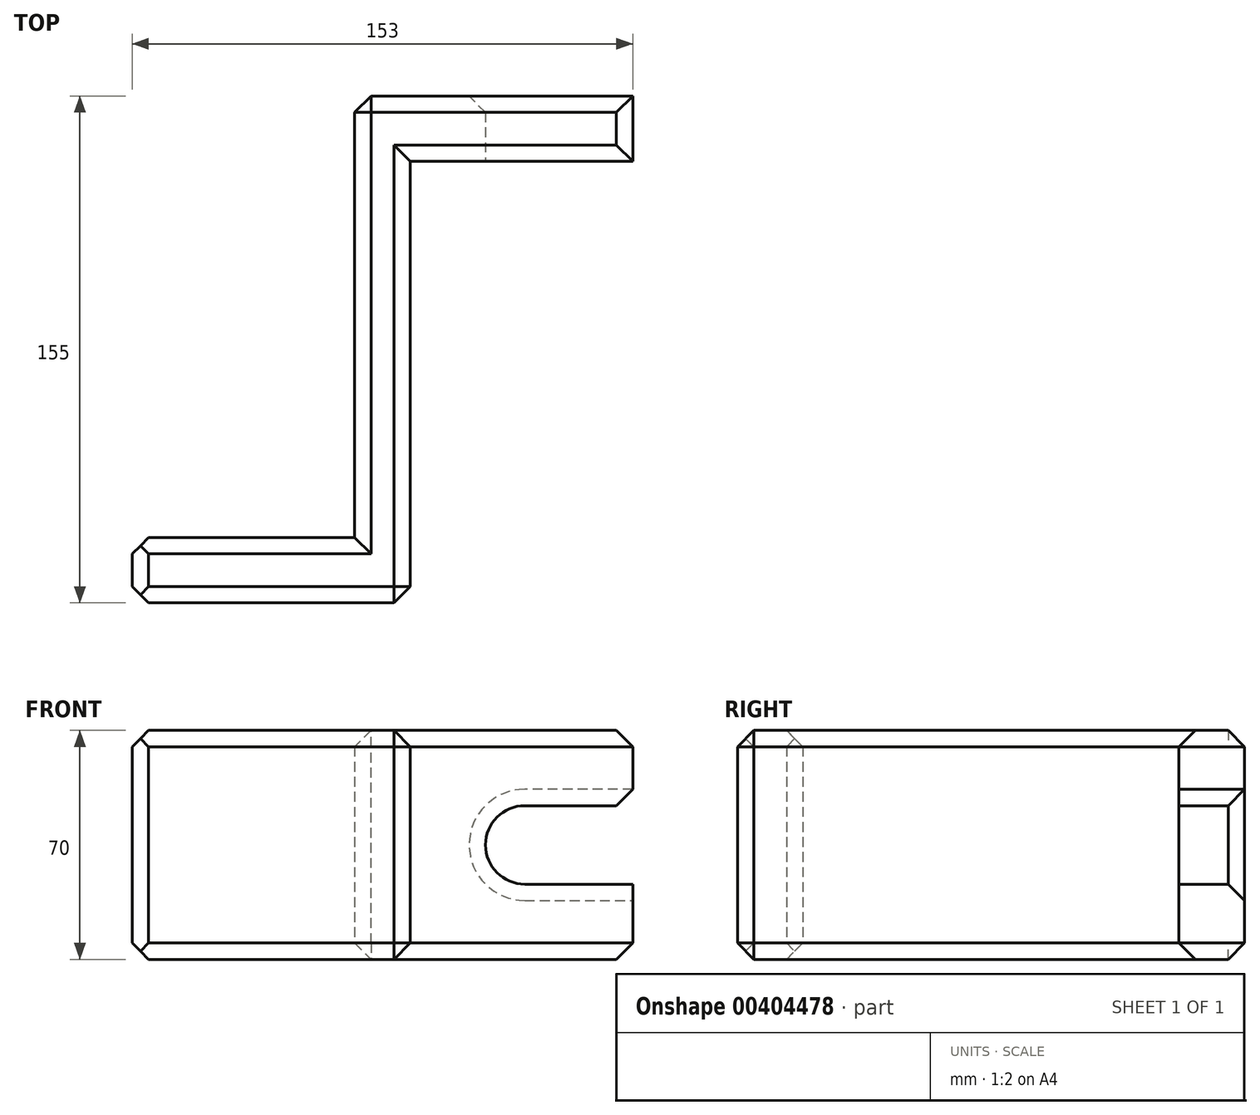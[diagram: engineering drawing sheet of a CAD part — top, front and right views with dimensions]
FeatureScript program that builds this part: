
annotation { "Feature Type Name" : "Feature", "Feature Type Description" : "" }
export const myFeature = defineFeature(function(context is Context, id is Id, definition is map)
    precondition{}
    {
        {
            var Q0;
            Q0=qCreatedBy(makeId("Top.planeOp"),FACE);
            var sketch = newSketch(context, id + "F0", { "sketchPlane" : qUnion([Q0])});
            skLineSegment(sketch, "E0.bottom", {"start": v(8.5, 57.5) * mm, "end": v(-8.5, 57.5) * mm});
            skLineSegment(sketch, "E0.top", {"start": v(8.5, -57.5) * mm, "end": v(-8.5, -57.5) * mm});
            skLineSegment(sketch, "E0.left", {"start": v(8.5, 57.5) * mm, "end": v(8.5, -57.5) * mm});
            skLineSegment(sketch, "E0.right", {"start": v(-8.5, 57.5) * mm, "end": v(-8.5, -57.5) * mm});
            skPoint(sketch, "E0.middle", {"position": v(0, 0) * mm});
            skLineSegment(sketch, "E1.bottom", {"start": v(8.5, -57.5) * mm, "end": v(-76.5, -57.5) * mm});
            skLineSegment(sketch, "E1.top", {"start": v(8.5, -77.5) * mm, "end": v(-76.5, -77.5) * mm});
            skLineSegment(sketch, "E1.left", {"start": v(8.5, -57.5) * mm, "end": v(8.5, -77.5) * mm});
            skLineSegment(sketch, "E1.right", {"start": v(-76.5, -57.5) * mm, "end": v(-76.5, -77.5) * mm});
            skLineSegment(sketch, "E2.bottom", {"start": v(-8.5, 57.5) * mm, "end": v(8.5, 57.5) * mm});
            skLineSegment(sketch, "E2.top", {"start": v(-8.5, 77.5) * mm, "end": v(76.5, 77.5) * mm});
            skLineSegment(sketch, "E2.left", {"start": v(-8.5, 57.5) * mm, "end": v(-8.5, 77.5) * mm});
            skLineSegment(sketch, "E2.right", {"start": v(76.5, 57.5) * mm, "end": v(76.5, 77.5) * mm});
            skLineSegment(sketch, "E3", {"start": v(8.5, 57.5) * mm, "end": v(76.5, 57.5) * mm});
            skSolve(sketch);
        }
        {
            var Q0;
            Q0 = qSketchRegion(id + "F0", true);
            extrude(context, id + "F1", {"entities" : qUnion([Q0]), "depth" : 70 * mm});
        }
        {
            var Q0;
            Q0=makeQuery(id+"F1.opExtrude","SWEPT_EDGE",EDGE,{"disambiguationData":[OSD([sQuery(id+"F0.wireOp",EDGE,"E2.top"),sQuery(id+"F0.wireOp",EDGE,"E2.left")])]});
            var Q1;
            Q1=makeQuery(id+"F1.opExtrude","CAP_EDGE",EDGE,{"disambiguationData":[OSD([sQuery(id+"F0.wireOp",EDGE,"E0.right"),sQuery(id+"F0.wireOp",EDGE,"E2.left")])],"isStart":false});
            var Q2;
            Q2=makeQuery(id+"F1.opExtrude","CAP_EDGE",EDGE,{"disambiguationData":[OSD([sQuery(id+"F0.wireOp",EDGE,"E2.top")])],"isStart":false});
            var Q3;
            Q3=makeQuery(id+"F1.opExtrude","CAP_EDGE",EDGE,{"disambiguationData":[OSD([sQuery(id+"F0.wireOp",EDGE,"E1.bottom")])],"isStart":false});
            var Q4;
            Q4=makeQuery(id+"F1.opExtrude","CAP_EDGE",EDGE,{"disambiguationData":[OSD([sQuery(id+"F0.wireOp",EDGE,"E0.left"),sQuery(id+"F0.wireOp",EDGE,"E1.left")])],"isStart":false});
            var Q5;
            Q5=makeQuery(id+"F1.opExtrude","CAP_EDGE",EDGE,{"disambiguationData":[OSD([sQuery(id+"F0.wireOp",EDGE,"E1.top")])],"isStart":false});
            var Q6;
            Q6=makeQuery(id+"F1.opExtrude","CAP_EDGE",EDGE,{"disambiguationData":[OSD([sQuery(id+"F0.wireOp",EDGE,"E3")])],"isStart":false});
            var Q7;
            Q7=makeQuery(id+"F1.opExtrude","CAP_EDGE",EDGE,{"disambiguationData":[OSD([sQuery(id+"F0.wireOp",EDGE,"E2.top")])],"isStart":true});
            var Q8;
            Q8=makeQuery(id+"F1.opExtrude","CAP_EDGE",EDGE,{"disambiguationData":[OSD([sQuery(id+"F0.wireOp",EDGE,"E3")])],"isStart":true});
            var Q9;
            Q9=makeQuery(id+"F1.opExtrude","CAP_EDGE",EDGE,{"disambiguationData":[OSD([sQuery(id+"F0.wireOp",EDGE,"E0.left"),sQuery(id+"F0.wireOp",EDGE,"E1.left")])],"isStart":true});
            var Q10;
            Q10=makeQuery(id+"F1.opExtrude","CAP_EDGE",EDGE,{"disambiguationData":[OSD([sQuery(id+"F0.wireOp",EDGE,"E1.top")])],"isStart":true});
            var Q11;
            Q11=makeQuery(id+"F1.opExtrude","SWEPT_EDGE",EDGE,{"disambiguationData":[OSD([sQuery(id+"F0.wireOp",EDGE,"E1.top"),sQuery(id+"F0.wireOp",EDGE,"E1.left")])]});
            var Q12;
            Q12=makeQuery(id+"F1.opExtrude","CAP_EDGE",EDGE,{"disambiguationData":[OSD([sQuery(id+"F0.wireOp",EDGE,"E1.bottom")])],"isStart":true});
            var Q13;
            Q13=makeQuery(id+"F1.opExtrude","CAP_EDGE",EDGE,{"disambiguationData":[OSD([sQuery(id+"F0.wireOp",EDGE,"E0.right"),sQuery(id+"F0.wireOp",EDGE,"E2.left")])],"isStart":true});
            chamfer(context, id + "F2", {"entities" : qUnion([Q0, Q1, Q2, Q3, Q4, Q5, Q6, Q7, Q8, Q9, Q10, Q11, Q12, Q13]), "width" : 5 * mm, "tangentPropagation" : true});
        }
        {
            var Q0;
            Q0=makeQuery(id+"F1.opExtrude","SWEPT_FACE",FACE,{"disambiguationData":[OSD([sQuery(id+"F0.wireOp",EDGE,"E3")])]});
            var sketch = newSketch(context, id + "F3", { "sketchPlane" : qUnion([Q0])});
            skLineSegment(sketch, "E4", {"start": v(76.5, 35) * mm, "end": v(8.5, 35) * mm, "construction": true});
            skCircle(sketch, "E5", {"center": v(43.5, 35) * mm, "radius": 12 * mm});
            skLineSegment(sketch, "E6.bottom", {"start": v(43.5, 47) * mm, "end": v(76.5, 47) * mm});
            skLineSegment(sketch, "E6.top", {"start": v(43.5, 23) * mm, "end": v(76.5, 23) * mm});
            skLineSegment(sketch, "E6.left", {"start": v(43.5, 47) * mm, "end": v(43.5, 23) * mm});
            skLineSegment(sketch, "E6.right", {"start": v(76.5, 47) * mm, "end": v(76.5, 23) * mm});
            skSolve(sketch);
        }
        {
            var Q0;
            {var subQ0=sQuery(id+"F3.wireOp",EDGE,"E6.left");Q0=makeQuery(id+"F3.imprint","IMPRINT",FACE,{"disambiguationData":[TD([[makeQuery(id+"F3.imprint","IMPRINT",EDGE,{"derivedFrom":subQ0}),-1.0]])]});}
            var Q1;
            {var subQ0=sQuery(id+"F3.wireOp",EDGE,"E6.left");Q1=makeQuery(id+"F3.imprint","IMPRINT",FACE,{"disambiguationData":[TD([[makeQuery(id+"F3.imprint","IMPRINT",EDGE,{"derivedFrom":subQ0}),1.0]])]});}
            var Q2;
            {var subQ1=sQuery(id+"F3.wireOp",EDGE,"E6.bottom");Q2=makeQuery(id+"F3.imprint","IMPRINT",FACE,{"disambiguationData":[TD([[makeQuery(id+"F3.imprint","IMPRINT",EDGE,{"derivedFrom":subQ1}),-1.0]])]});}
            extrude(context, id + "F4", {"entities" : qUnion([Q0, Q1, Q2]), "operationType" : NewBodyOperationType.REMOVE, "endBound" : BoundingType.THROUGH_ALL, "oppositeDirection" : true, "depth" : 25 * mm});
        }
        {
            var Q0;
            Q0=makeQuery(id+"F4.boolean.opBoolean","COPY",EDGE,{"derivedFrom":makeQuery(id+"F4.opExtrude","CAP_EDGE",EDGE,{"disambiguationData":[OSD([sQuery(id+"F3.wireOp",EDGE,"E5")])],"isStart":true})});
            var Q1;
            Q1=makeQuery(id+"F4.boolean.opBoolean","INTERSECT",EDGE,{"derivedFrom":[makeQuery(id+"F1.opExtrude","SWEPT_FACE",FACE,{"disambiguationData":[OSD([sQuery(id+"F0.wireOp",EDGE,"E2.top")])]}),makeQuery(id+"F4.opExtrude","SWEPT_FACE",FACE,{"disambiguationData":[OSD([sQuery(id+"F3.wireOp",EDGE,"E5")])]})]});
            var Q2;
            Q2=makeQuery(id+"F4.boolean.opBoolean","COPY",EDGE,{"derivedFrom":makeQuery(id+"F4.opExtrude","SWEPT_EDGE",EDGE,{"disambiguationData":[OSD([sQuery(id+"F0.wireOp",EDGE,"E2.right"),sQuery(id+"F0.wireOp",EDGE,"E3"),sQuery(id+"F3.wireOp",EDGE,"E6.bottom"),sQuery(id+"F3.wireOp",EDGE,"E6.right")])]})});
            var Q3;
            Q3=makeQuery(id+"F4.boolean.opBoolean","COPY",EDGE,{"derivedFrom":makeQuery(id+"F4.opExtrude","SWEPT_EDGE",EDGE,{"disambiguationData":[OSD([sQuery(id+"F0.wireOp",EDGE,"E2.right"),sQuery(id+"F0.wireOp",EDGE,"E3"),sQuery(id+"F3.wireOp",EDGE,"E6.top"),sQuery(id+"F3.wireOp",EDGE,"E6.right")])]})});
            chamfer(context, id + "F5", {"entities" : qUnion([Q0, Q1, Q2, Q3]), "width" : 5 * mm, "tangentPropagation" : true});
        }
        {
            var Q0;
            Q0=makeQuery(id+"F1.opExtrude","CAP_EDGE",EDGE,{"disambiguationData":[OSD([sQuery(id+"F0.wireOp",EDGE,"E2.right")])],"isStart":false});
            var Q1;
            Q1=makeQuery(id+"F1.opExtrude","CAP_EDGE",EDGE,{"disambiguationData":[OSD([sQuery(id+"F0.wireOp",EDGE,"E2.right")])],"isStart":true});
            var Q2;
            Q2=makeQuery(id+"F1.opExtrude","SWEPT_EDGE",EDGE,{"disambiguationData":[OSD([sQuery(id+"F0.wireOp",EDGE,"E1.bottom"),sQuery(id+"F0.wireOp",EDGE,"E1.right")])]});
            var Q3;
            Q3=makeQuery(id+"F1.opExtrude","SWEPT_EDGE",EDGE,{"disambiguationData":[OSD([sQuery(id+"F0.wireOp",EDGE,"E1.top"),sQuery(id+"F0.wireOp",EDGE,"E1.right")])]});
            var Q4;
            Q4=makeQuery(id+"F1.opExtrude","CAP_EDGE",EDGE,{"disambiguationData":[OSD([sQuery(id+"F0.wireOp",EDGE,"E1.right")])],"isStart":true});
            var Q5;
            Q5=makeQuery(id+"F1.opExtrude","CAP_EDGE",EDGE,{"disambiguationData":[OSD([sQuery(id+"F0.wireOp",EDGE,"E1.right")])],"isStart":false});
            chamfer(context, id + "F6", {"entities" : qUnion([Q0, Q1, Q2, Q3, Q4, Q5]), "width" : 5 * mm, "tangentPropagation" : true});
        }
    });
